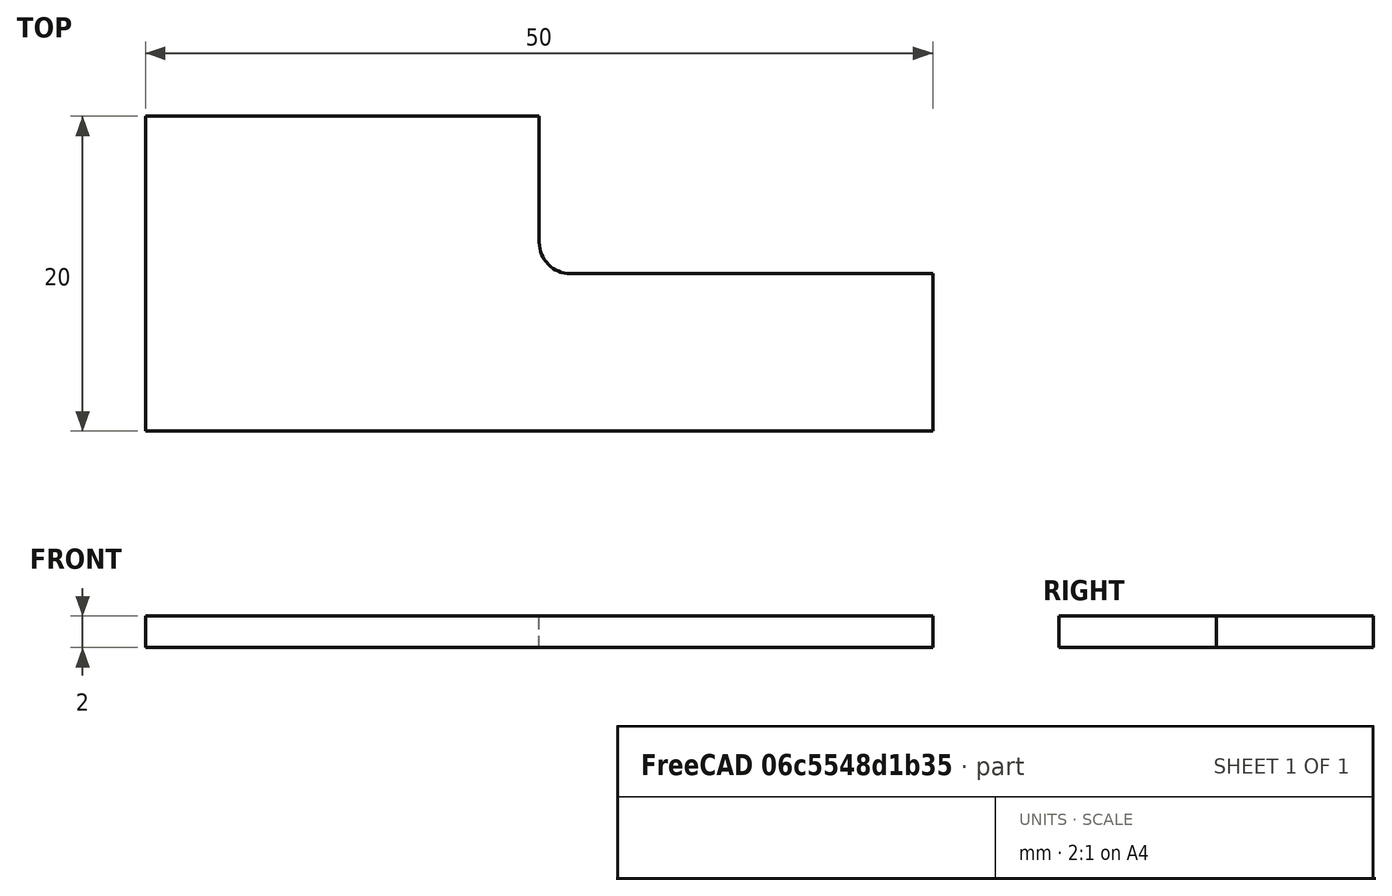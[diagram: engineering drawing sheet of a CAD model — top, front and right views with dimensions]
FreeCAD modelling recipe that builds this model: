
FCSTD DOCUMENT  (FreeCAD 0.18R15860 (Git))
Label: geometry
License: All rights reserved
LicenseURL: http://en.wikipedia.org/wiki/All_rights_reserved
objects: Fem::ConstraintDisplacement×3, Sketcher::SketchObject×1, PartDesign::Pad×1, PartDesign::Body×1, Fem::FemSolverObjectPython×1, Fem::ConstraintPressure×1, App::MaterialObjectPython×1, Fem::FemMeshShapeNetgenObject×1, Fem::FemSetNodesObject×1, Fem::FemMeshObjectPython×1, Fem::FemResultObjectPython×1, Fem::FemAnalysis×1
note: 4 computed .brp shape members not serialized (recipe doc carries the construction recipe); baked Part::Feature solids carry a one-line shape summary decoded from their .brp

FEATURE [Sketcher::SketchObject] Sketch
  MapMode = 5
  Support = -> [XY_Plane]
  sketch-geometry (7):
    g0: LineSegment StartX=0 StartY=0 StartZ=0 EndX=50 EndY=0 EndZ=0
    g1: LineSegment StartX=50 StartY=0 StartZ=0 EndX=50 EndY=10 EndZ=0
    g2: LineSegment StartX=50 StartY=10 StartZ=0 EndX=27 EndY=10 EndZ=0
    g3: LineSegment StartX=25 StartY=12 StartZ=0 EndX=25 EndY=20 EndZ=0
    g4: LineSegment StartX=25 StartY=20 StartZ=0 EndX=0 EndY=20 EndZ=0
    g5: LineSegment StartX=0 StartY=20 StartZ=0 EndX=0 EndY=0 EndZ=0
    g6: ArcOfCircle CenterX=27 CenterY=12 CenterZ=0 NormalX=0 NormalY=0 NormalZ=1 AngleXU=0 Radius=2 StartAngle=3.14159 EndAngle=4.71239
  constraints (19):
    c: Coincident(g-1,g0)
    c: PointOnObject(g0,g-1)
    c: Coincident(g0,g1)
    c: Vertical(g1)
    c: Coincident(g1,g2)
    c: Horizontal(g2)
    c: Vertical(g3)
    c: Coincident(g3,g4)
    c: PointOnObject(g4,g-2)
    c: Horizontal(g4)
    c: Coincident(g4,g5)
    c: Coincident(g5,g0)
    c: DistanceY(g5,g5) = 20
    c: DistanceY(g1,g1) = 10
    c: DistanceX(g0,g0) = 50
    c: DistanceX(g4,g4) = 25
    c: Tangent(g2,g6) = 1.5708
    c: Tangent(g3,g6) = 1.5708
    c: Radius(g6) = 2
FEATURE [PartDesign::Pad] Pad
  Length = 2
  Length2 = 100
  Profile = -> Sketch
  Type = 0
FEATURE [PartDesign::Body] Body
  Group = -> [Sketch,Pad]
  Origin = -> Origin
  Tip = -> Pad
FEATURE [Fem::FemSolverObjectPython] CalculiXccxTools  # FEM object (typed FeaturePython)
  AnalysisType = 0
  BeamShellResultOutput3D = false
  EigenmodeHighLimit = 1000000
  EigenmodeLowLimit = 0
  EigenmodesCount = 10
  GeometricalNonlinearity = 0
  IterationsControlParameterCutb = 0.25,0.5,0.75,0.85,,,1.5,
  IterationsControlParameterIter = 4,8,9,200,10,400,,200,,
  IterationsControlParameterTimeUse = false
  IterationsThermoMechMaximum = 2000
  IterationsUserDefinedIncrementations = false
  IterationsUserDefinedTimeStepLength = false
  MaterialNonlinearity = 0
  MatrixSolverType = 0
  SplitInputWriter = false
  ThermoMechSteadyState = true
  TimeEnd = 1
  TimeInitialStep = 0.01
FEATURE [Fem::ConstraintPressure] FemConstraintPressure
  NormalDirection = (1,0,0)
  Normals = (9) [(1,0,0),(1,0,0),(1,0,0),(1,0,0),(1,0,0),(1,0,0),(1,0,0),(1,0,0),(1,0,0)]
  Points = (9) [(50,0,2),(50,5,2),(50,10,2),(50,0,1),(50,5,1),(50,10,1),(50,0,0),(50,5,0),(50,10,0)]
  Pressure = 100
  References = -> [Pad]
  Reversed = true
FEATURE [App::MaterialObjectPython] SolidMaterial  # material (typed FeaturePython)
  Category = 0
  Material = Density=7900.000000000001 kg/m^3,Description=Standard steel material for CalculiX sample calculations,Father=Metal,Name=CalculiX-Steel,+5 more (map truncated)
FEATURE [Fem::ConstraintDisplacement] FemConstraintDisplacement
  NormalDirection = (0,-1,0)
  Normals = (12) [(0,-1,0),(0,-1,0),(0,-1,0),(0,-1,0),(0,-1,0),(0,-1,0),(0,-1,0),(0,-1,0),(0,-1,0),(0,-1,0),(0,-1,0),(0,-1,0)]
  Points = (12) [(0,0,2),(16.6667,0,2),(33.3333,0,2),(50,0,2),(0,0,1),(16.6667,0,1),(33.3333,0,1),(50,0,1),(0,0,0),(16.6667,0,0),(33.3333,0,0),(50,0,0)]
  References = -> [Pad]
  Scale = 3
  rotxFix = false
  rotxFree = true
  rotyFix = false
  rotyFree = true
  rotzFix = false
  rotzFree = true
  xDisplacement = 0
  xFix = false
  xFree = true
  xRotation = 0
  yDisplacement = 0
  yFix = true
  yFree = false
  yRotation = 0
  zDisplacement = 0
  zFix = false
  zFree = true
  zRotation = 0
FEATURE [Fem::ConstraintDisplacement] FemConstraintDisplacement001
  NormalDirection = (-1,0,0)
  Normals = (9) [(-1,0,0),(-1,0,0),(-1,0,0),(-1,0,0),(-1,0,0),(-1,0,0),(-1,0,0),(-1,0,0),(-1,0,0)]
  Points = (9) [(0,20,2),(0,10,2),(0,0,2),(0,20,1),(0,10,1),(0,0,1),(0,20,0),(0,10,0),(0,0,0)]
  References = -> [Pad]
  rotxFix = false
  rotxFree = true
  rotyFix = false
  rotyFree = true
  rotzFix = false
  rotzFree = true
  xDisplacement = 0
  xFix = true
  xFree = false
  xRotation = 0
  yDisplacement = 0
  yFix = false
  yFree = true
  yRotation = 0
  zDisplacement = 0
  zFix = false
  zFree = true
  zRotation = 0
FEATURE [Fem::ConstraintDisplacement] FemConstraintDisplacement002
  NormalDirection = (0,0,-1)
  Normals = (20) [(0,0,-1),(0,0,-1),(0,0,-1),(0,0,-1),(0,0,-1),(0,0,-1),(0,0,-1),(0,0,-1),(0,0,-1),(0,0,-1),(0,0,1),(0,0,1),(0,0,1),(0,0,1),(0,0,1),(0,0,1),(0,0,1),+3 more]
  Points = (20) [(0,0,0),(16.6667,0,0),(33.3333,0,0),(50,0,0),(0,10,0),(16.6667,10,0),(33.3333,10,0),(50,10,0),(0,20,0),(16.6667,20,0),(0,0,2),(16.6667,0,2),+8 more]
  References = -> [Pad]
  Scale = 4
  rotxFix = false
  rotxFree = true
  rotyFix = false
  rotyFree = true
  rotzFix = false
  rotzFree = true
  xDisplacement = 0
  xFix = false
  xFree = true
  xRotation = 0
  yDisplacement = 0
  yFix = false
  yFree = true
  yRotation = 0
  zDisplacement = 0
  zFix = true
  zFree = false
  zRotation = 0
FEATURE [Fem::FemMeshShapeNetgenObject] FEMMeshNetgen
  Fineness = 2
  GrowthRate = 0.3
  MaxSize = 2
  NbSegsPerEdge = 1
  NbSegsPerRadius = 2
  Optimize = true
  SecondOrder = true
  Shape = -> Pad
FEATURE [Fem::FemSetNodesObject] NodesSet
  FemMesh = -> FEMMeshNetgen
FEATURE [Fem::FemMeshObjectPython] Result_mesh  # FEM object (typed FeaturePython)
FEATURE [Fem::FemResultObjectPython] CalculiX_static_results  # FEM object (typed FeaturePython)
  DisplacementLengths = [0.00779753,0.00780379,0.0182211,0.018221,0.0180904,0.0180903,0,0,0.00244253,0.0024424,0.00193145,0.00193068,0.00471071,0.00470988,0.00384428,0.00305672,0.0024632,0.00212407,0.00240715,0.00267542,0.00286576,0.00296389,0.00298025,0.00293387,+3048 more]
  DisplacementVectors = (3072) [(0.00774146,-0.000933413,0),(0.00774802,-0.000931306,0),(0.0181244,-0.00187481,0),(0.0181243,-0.00187479,0),(0.0180904,0,0),(0.0180903,0,0),(0,0,0),+3065 more]
  Eigenmode = 0
  EigenmodeFrequency = 0
  MaxShear = [96.3256,97.615,50.0091,49.9932,50.4158,50.4072,36.8324,36.8439,19.2066,19.2726,0.131803,0.166733,15.1821,15.0302,1.53435,4.38682,2.05146,1.72761,2.67408,1.59646,1.09278,4.45026,7.83614,10.8988,13.4942,15.5841,17.1742,18.2771,18.9464,+3043 more]
  Mesh = -> Result_mesh
  NodeNumbers = [1,2,3,4,5,6,7,8,9,10,11,12,13,14,15,16,17,18,19,20,21,22,23,24,25,26,27,28,29,30,31,32,33,34,35,36,37,38,39,40,41,42,43,44,45,46,47,48,49,50,51,52,53,54,55,56,57,58,59,60,61,62,63,64,65,66,67,68,69,+3003 more]
  PrincipalMax = [196.668,199.237,100.027,100.011,99.999,99.9958,60.9406,60.9452,38.4376,38.5325,0.214168,-0.0956391,28.6173,28.3848,-1.13057,-0.650855,-0.0394735,-0.0220867,-0.147344,-0.121702,2.12744,8.90887,15.7155,21.8554,27.0503,31.2295,34.4094,36.617,+3044 more]
  PrincipalMed = [59.4138,60.3329,30.0098,30.0105,29.7513,29.7514,14.4661,14.4632,11.5446,11.5477,0.0111766,-0.1145,8.54461,8.56977,-1.4312,-3.01808,-1.21303,-1.05526,-1.69841,-1.03707,0.618577,2.67602,4.7294,6.57591,8.13569,9.38773,10.3398,11.0093,11.4132,+3043 more]
  PrincipalMin = [4.01728,4.00699,0.00881994,0.0246016,-0.832557,-0.818618,-12.7242,-12.7427,0.0243827,-0.012692,-0.0494373,-0.429105,-1.74685,-1.67554,-4.19927,-9.4245,-4.14239,-3.47731,-5.4955,-3.31462,-0.0581184,0.00834594,0.0432567,0.057944,0.0618575,+3047 more]
  ResultType = Fem::FemResultMechanical
  Stats = [0,0.00619873,0.0181244,-0.0024577,-0.0011157,0,-2.95681e-06,-1.78698e-09,2.11315e-06,0,0.00656783,0.0182211,0.239131,62.3244,208.978,-1.13057,68.8528,246.2,-3.01808,20.2655,78.8967,-12.8539,-1.30485,37.5453,0.131803,35.0788,116.999,0,0,0,0,+8 more]
  StrainVectors = (3072) [(0.000822923,-0.000323734,-3.76237e-06),(0.000835779,-0.00033068,-3.04837e-06),(0.000433433,-0.000185724,-3.84702e-09),+3069 more]
  StressValues = [171.788,174.043,88.8991,88.8721,89.5464,89.5331,64.5202,64.5392,34.1433,34.2604,0.239131,0.324447,26.7471,26.4691,2.92998,7.86203,3.66008,3.07184,4.76584,2.8478,1.93794,7.91152,13.9333,19.3788,23.993,27.7084,30.5353,32.4946,33.6887,34.7438,+3042 more]
  StressVectors = (3072) [(192.957,7.72739,59.4151),(195.836,7.40788,60.333),(100.027,0.00882396,30.0098),(100.011,0.0246119,30.0105),(99.999,-0.832557,29.7513),+3067 more]
  Time = 0
FEATURE [Fem::FemAnalysis] Analysis
  Group = -> [CalculiXccxTools,FemConstraintPressure,SolidMaterial,FemConstraintDisplacement,FemConstraintDisplacement001,FemConstraintDisplacement002,FEMMeshNetgen,CalculiX_static_results]
